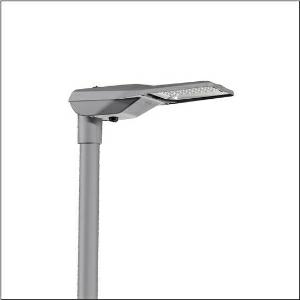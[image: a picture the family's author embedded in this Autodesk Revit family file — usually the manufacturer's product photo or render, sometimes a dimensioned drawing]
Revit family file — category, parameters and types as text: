
# Revit family: streetlight_sl_21_iq_mini___st1_5a_5xe2p31y08gb_2fd1
name_source: partatom
category: Lighting Fixtures
units: mm (PartAtom-declared; Revit-internal decimal feet)

## family parameters
Cut with Voids When Loaded = No
Host = Face
Light Source = No
Part Type = Normal
Room Calculation Point = No
Round Connector Dimension = Use Diameter
Shared = No

## types (1)
- --- (1 x LED, 5880 lm, 39.8 W, 3000K)
    Apparent Load = 40 VA
    CIE Flux Codes = 22 53 95 100 100
    Color Rendering = 70
    Color Temperature = 3000K
    Default Elevation = 1800 mm
    Description = Streetlight SL 21 iQ mini, mast luminaire, primary light control with lens, of PMMA, primary optical cover: cover, of toughened safety glass, transparent, light distribution: ST1.5a, light emission: direct distribution, primary light characteristic: asymmetric, installation type: post-top, side-entry, LED, High Power LED, rated luminous flux: 5.880lm, luminous efficacy: 148lm/W, light colour: 730, colour temperature: 3000K, control gear: iQ-Street Remote, D4i with power reduction, control: pre-setting: logarithmic dimming characteristic, Street-Remote, Auto-Match, Temp-Guard, Lumen-Switch, Night-Set, Smart-Wire, Light-Fading, Desk-Remote (wireless, voltage-free reading and setting of iQ features in the workshop via application-optimized NFC function/RFID function), optimised constant luminous flux control (CLO 2.0), mains connection: 220..240V, AC, 50/60Hz, start of lifetime: 40W, end of service life: 41W, reduction: 18W, luminaire housing, of diecast aluminium, powder-coated, SITECO metallic grey (DB 702S), corrosivity category C5 high according to DIN EN ISO 12944, please order mast flange separately, inclination adjustable: 0°, 5°, 10°, 15°, sealing non-destructively replaceable, multi-level sealing system, length: 628mm, width: 235mm, height: 110mm, mast flange for spigot size: 42mm (side-entry): 5XC10008XM4, 60/48mm (side-entry/post-top): 5XC10108XM2, 76/60mm (side-entry/post-top): 5XC10108XM1, mounting height: 4..8m, Smart Interface below and above, protection rating (complete): IP66, insulation class (complete): insulation class II (safety insulation), certification: CE, ENEC, ENEC+, VDE, impact resistance: IK10, permissible operating ambient temperature for outdoor applications: -40..+50°C, standard-compliant lighting for roads and squares, packaging unit: 1 piece

Light Distribution: ST1.5a
    Height = 110 mm
    Lamp = 1 x LED
    Lamp Light Flux = 5880 lm
    Lamp Power = 39.8 W
    Lamp count = 1
    Length = 625 mm
    Luminous efficacy = 148 lm/W
    Manufacturer = Siteco
    ModVariant = No
    Model = 5XE2P31Y08GB
    Number of Poles = 1
    OnlyDefault = Yes
    Power Factor = 1
    Product Name = Streetlight SL 21 iQ mini | ST1.5a
    Product group = mast luminaire | pylon top
    ProductGroupID = 6100
    Protection Class = Protection class II
    Protection Degree = IP 66
    RLX_Detail_Level = 1
    RLX_Emergency_Light_Flux = 0 lm
    RLX_Emergency_Type = 0
    RLX_Emergency_Type_DB = No
    RlxData = <blob elided: 96417 chars, md5=2c262a75>
    Socket = socket
    Standby Power = 0 W
    System Light Flux = 5880 lm
    System Power = 40 W
    Type Comments = factory setting: luminous flux: 100 % | dim-lin: 254 | 800 mA
    Type Image = l_1003514.jpg
    URL = http://relux.com
    VarID = @adj_111889
    Voltage = 0 V
    Weight = 0.00 kg
    Width = 234 mm

## geometry (parser evidence)
native form markers: Blend x4, Sweep x11
no freeform markers — native parametric forms only
